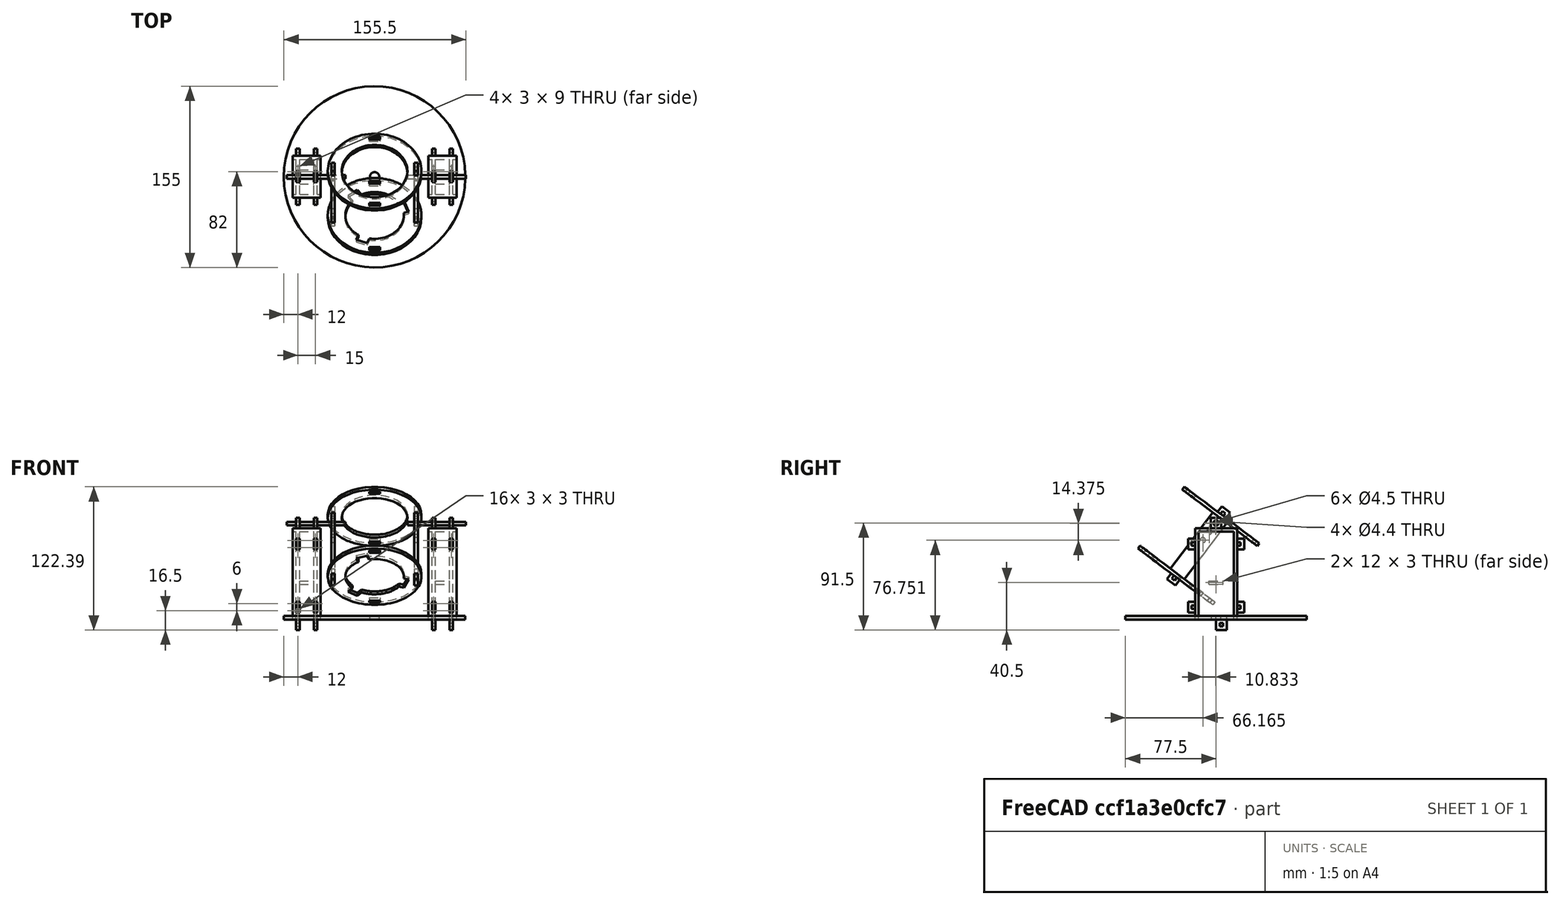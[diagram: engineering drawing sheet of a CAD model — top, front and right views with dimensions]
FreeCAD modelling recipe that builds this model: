
FCSTD DOCUMENT  (FreeCAD 0.16R6707 (Git))
Label: turretComplete
License: All rights reserved
LicenseURL: http://en.wikipedia.org/wiki/All_rights_reserved
objects: Part::Box×113, Part::Cut×80, Part::MultiFuse×19, Part::Cylinder×18
note: 230 computed .brp shape members not serialized (recipe doc carries the construction recipe); baked Part::Feature solids carry a one-line shape summary decoded from their .brp

FEATURE [Part::Cylinder] Cylinder
  Angle = 360
  Height = 3
  Radius = 77.5
FEATURE [Part::Cylinder] Cylinder017  label="Cylinder001"
  Angle = 360
  Height = 3
  Radius = 4
FEATURE [Part::Cut] Cut  label="cut002"
  Base = -> Cylinder
  Tool = -> Cylinder017
FEATURE [Part::Box] Box001  label="Cube001"
  Height = 3
  Length = 3
  Placement = pos=(-52,0,0) rot=(0,0,1;0rad)
  Width = 9
FEATURE [Part::Box] Box126  label="Cube048"
  Height = 3
  Length = 3
  Placement = pos=(-67,0,0) rot=(0,0,1;0rad)
  Width = 9
FEATURE [Part::Box] Box127  label="Cube049"
  Height = 3
  Length = 3
  Placement = pos=(49,0,0) rot=(0,0,1;0rad)
  Width = 9
FEATURE [Part::Box] Box128  label="Cube050"
  Height = 3
  Length = 3
  Placement = pos=(64,0,0) rot=(0,0,1;0rad)
  Width = 9
FEATURE [Part::Cut] Cut001
  Base = -> Cut
  Tool = -> Box126
FEATURE [Part::Cut] Cut002
  Base = -> Cut001
  Tool = -> Box001
FEATURE [Part::Cut] Cut003
  Base = -> Cut002
  Tool = -> Box128
FEATURE [Part::Cut] Cut004  label="turretBasis"
  Base = -> Cut003
  Tool = -> Box127
FEATURE [Part::Box] Box111  label="Cube033"
  Height = 3
  Length = 9
  Placement = pos=(1,12,15) rot=(0,0,1;0rad)
  Width = 3
FEATURE [Part::Box] Box112  label="Cube034"
  Height = 3
  Length = 9
  Placement = pos=(1,12,0) rot=(0,0,1;0rad)
  Width = 3
FEATURE [Part::Box] Box  label="Cube"
  Height = 12
  Length = 12
  Placement = pos=(-0.5,12,3) rot=(0,0,1;0rad)
  Width = 3
FEATURE [Part::MultiFuse] Fusion030  label="turretPitchHolderDistant"
  Placement = pos=(9.5,18,0) rot=(0,0,1;0rad)
  Shapes = -> [Box112,Box,Box111]
FEATURE [Part::Box] Box123  label="Cube045"
  Height = 3
  Length = 9
  Placement = pos=(10.5,-3,0) rot=(0,0,1;0rad)
  Width = 3
FEATURE [Part::Box] Box124  label="Cube046"
  Height = 24
  Length = 36
  Placement = pos=(-3,-3,-3) rot=(0,0,1;0rad)
  Width = 3
FEATURE [Part::Cut] Cut052
  Base = -> Box124
  Tool = -> Box123
FEATURE [Part::Box] Box125  label="Cube047"
  Height = 3
  Length = 9
  Placement = pos=(10.5,-3,15) rot=(0,0,1;0rad)
  Width = 3
FEATURE [Part::Cut] Cut058  label="turretPitchHolderTopPlate"
  Base = -> Cut052
  Placement = pos=(0,78,0) rot=(0,0,1;0rad)
  Tool = -> Box125
FEATURE [Part::Box] Box082  label="Cube006"
  Height = 3
  Length = 30
  Width = 75
FEATURE [Part::Box] Box129  label="Cube007"
  Height = 3
  Length = 9
  Placement = pos=(-9,6,0) rot=(0,0,1;0rad)
  Width = 9
FEATURE [Part::Box] Box002  label="Cube008"
  Height = 4
  Length = 3
  Placement = pos=(-6,9,0) rot=(0,0,1;0rad)
  Width = 3
FEATURE [Part::Cut] Cut034
  Base = -> Box129
  Tool = -> Box002
FEATURE [Part::Box] Box003  label="Cube009"
  Height = 3
  Length = 9
  Placement = pos=(-9,6,0) rot=(0,0,1;0rad)
  Width = 9
FEATURE [Part::Box] Box004  label="Cube010"
  Height = 4
  Length = 3
  Placement = pos=(-6,9,0) rot=(0,0,1;0rad)
  Width = 3
FEATURE [Part::Cut] Cut059
  Base = -> Box003
  Placement = pos=(39,0,0) rot=(0,0,1;0rad)
  Tool = -> Box004
FEATURE [Part::Box] Box005  label="Cube011"
  Height = 3
  Length = 9
  Placement = pos=(10.5,30,0) rot=(0,0,1;0rad)
  Width = 3
FEATURE [Part::Cut] Cut060
  Base = -> Box082
  Tool = -> Box005
FEATURE [Part::MultiFuse] Fusion027
  Shapes = -> [Cut034,Cut059,Cut060]
FEATURE [Part::Box] Box006  label="Cube012"
  Height = 3
  Length = 9
  Placement = pos=(10.5,36,0) rot=(0,0,1;0rad)
  Width = 9
FEATURE [Part::Cylinder] Cylinder027  label="RotationHoie"
  Angle = 360
  Height = 10
  Placement = pos=(15,40.5,0) rot=(0,0,1;0rad)
  Radius = 2.2
FEATURE [Part::Cut] Cut061
  Base = -> Box006
  Placement = pos=(0,42,0) rot=(0,0,1;0rad)
  Tool = -> Cylinder027
FEATURE [Part::Box] Box083  label="Cube013"
  Height = 3
  Length = 9
  Placement = pos=(-9,6,0) rot=(0,0,1;0rad)
  Width = 9
FEATURE [Part::Box] Box084  label="Cube014"
  Height = 4
  Length = 3
  Placement = pos=(-6,9,0) rot=(0,0,1;0rad)
  Width = 3
FEATURE [Part::Cut] Cut035
  Base = -> Box083
  Placement = pos=(24,-15,0) rot=(0,0,1;0rad)
  Tool = -> Box084
FEATURE [Part::Box] Box085  label="Cube015"
  Height = 3
  Length = 9
  Placement = pos=(-9,6,0) rot=(0,0,1;0rad)
  Width = 9
FEATURE [Part::Box] Box086  label="Cube016"
  Height = 4
  Length = 3
  Placement = pos=(-6,9,0) rot=(0,0,1;0rad)
  Width = 3
FEATURE [Part::Cut] Cut036
  Base = -> Box085
  Placement = pos=(39,54,0) rot=(0,0,1;0rad)
  Tool = -> Box086
FEATURE [Part::Box] Box087  label="Cube017"
  Height = 3
  Length = 9
  Placement = pos=(-9,6,0) rot=(0,0,1;0rad)
  Width = 9
FEATURE [Part::Box] Box088  label="Cube018"
  Height = 4
  Length = 3
  Placement = pos=(-6,9,0) rot=(0,0,1;0rad)
  Width = 3
FEATURE [Part::Cut] Cut037
  Base = -> Box087
  Placement = pos=(0,54,0) rot=(0,0,1;0rad)
  Tool = -> Box088
FEATURE [Part::MultiFuse] Fusion  label="Fusion001"
  Shapes = -> [Cut061,Cut035,Cut036,Cut037,Fusion027]
FEATURE [Part::Box] Box130  label="Cube051"
  Height = 3
  Length = 9
  Placement = pos=(10.5,75,0) rot=(0,0,1;0rad)
  Width = 3
FEATURE [Part::MultiFuse] Fusion031  label="turretPitchHolderSide"
  Shapes = -> [Fusion,Box130]
FEATURE [Part::Box] Box113  label="Cube035"
  Height = 3
  Length = 3
  Placement = pos=(30,60,0) rot=(0,0,1;0rad)
  Width = 9
FEATURE [Part::Box] Box114  label="Cube036"
  Height = 3
  Length = 3
  Placement = pos=(39,6,0) rot=(0,0,1;0rad)
  Width = 9
FEATURE [Part::Box] Box115  label="Cube037"
  Height = 3
  Length = 3
  Placement = pos=(39,6,15) rot=(0,0,1;0rad)
  Width = 9
FEATURE [Part::Box] Box116  label="Cube038"
  Height = 3
  Length = 3
  Placement = pos=(39,60,15) rot=(0,0,1;0rad)
  Width = 9
FEATURE [Part::Box] Box117  label="Cube039"
  Height = 24
  Length = 3
  Placement = pos=(39,0,-3) rot=(0,0,1;0rad)
  Width = 75
FEATURE [Part::Cut] Cut062
  Base = -> Box117
  Tool = -> Box116
FEATURE [Part::Cut] Cut045
  Base = -> Cut062
  Tool = -> Box115
FEATURE [Part::Cut] Cut046
  Base = -> Cut045
  Tool = -> Box114
FEATURE [Part::Cut] Cut047  label="Cutx058"
  Base = -> Cut046
  Placement = pos=(-9,0,0) rot=(0,0,1;0rad)
  Tool = -> Box113
FEATURE [Part::Cut] Cut063  label="turretPitchHolderSidePlate"
  Base = -> Cut047
  Tool = -> Box113
FEATURE [Part::Box] Box131  label="Cube052"
  Height = 3
  Length = 3
  Placement = pos=(30,60,0) rot=(0,0,1;0rad)
  Width = 9
FEATURE [Part::Box] Box132  label="Cube053"
  Height = 3
  Length = 3
  Placement = pos=(39,6,0) rot=(0,0,1;0rad)
  Width = 9
FEATURE [Part::Box] Box133  label="Cube054"
  Height = 3
  Length = 3
  Placement = pos=(39,6,15) rot=(0,0,1;0rad)
  Width = 9
FEATURE [Part::Box] Box134  label="Cube055"
  Height = 3
  Length = 3
  Placement = pos=(39,60,15) rot=(0,0,1;0rad)
  Width = 9
FEATURE [Part::Box] Box135  label="Cube056"
  Height = 24
  Length = 3
  Placement = pos=(39,0,-3) rot=(0,0,1;0rad)
  Width = 75
FEATURE [Part::Cut] Cut064
  Base = -> Box135
  Tool = -> Box134
FEATURE [Part::Cut] Cut065
  Base = -> Cut064
  Tool = -> Box133
FEATURE [Part::Cut] Cut066
  Base = -> Cut065
  Tool = -> Box132
FEATURE [Part::Cut] Cut067  label="Cutx059"
  Base = -> Cut066
  Placement = pos=(-9,0,0) rot=(0,0,1;0rad)
  Tool = -> Box131
FEATURE [Part::Cut] Cut068  label="turretPitchHolderSidePlate001"
  Base = -> Cut067
  Placement = pos=(-33,0,0) rot=(0,0,1;0rad)
  Tool = -> Box131
FEATURE [Part::Box] Box136  label="Cube057"
  Height = 3
  Length = 30
  Width = 75
FEATURE [Part::Box] Box137  label="Cube058"
  Height = 3
  Length = 9
  Placement = pos=(-9,6,0) rot=(0,0,1;0rad)
  Width = 9
FEATURE [Part::Box] Box138  label="Cube059"
  Height = 4
  Length = 3
  Placement = pos=(-6,9,0) rot=(0,0,1;0rad)
  Width = 3
FEATURE [Part::Cut] Cut069
  Base = -> Box137
  Tool = -> Box138
FEATURE [Part::Box] Box139  label="Cube060"
  Height = 3
  Length = 9
  Placement = pos=(-9,6,0) rot=(0,0,1;0rad)
  Width = 9
FEATURE [Part::Box] Box140  label="Cube061"
  Height = 4
  Length = 3
  Placement = pos=(-6,9,0) rot=(0,0,1;0rad)
  Width = 3
FEATURE [Part::Cut] Cut070
  Base = -> Box139
  Placement = pos=(39,0,0) rot=(0,0,1;0rad)
  Tool = -> Box140
FEATURE [Part::Box] Box141  label="Cube062"
  Height = 3
  Length = 9
  Placement = pos=(10.5,30,0) rot=(0,0,1;0rad)
  Width = 3
FEATURE [Part::Cut] Cut071
  Base = -> Box136
  Tool = -> Box141
FEATURE [Part::MultiFuse] Fusion032
  Shapes = -> [Cut069,Cut070,Cut071]
FEATURE [Part::Box] Box142  label="Cube063"
  Height = 3
  Length = 9
  Placement = pos=(10.5,36,0) rot=(0,0,1;0rad)
  Width = 9
FEATURE [Part::Cylinder] Cylinder028  label="RotationHoie001"
  Angle = 360
  Height = 10
  Placement = pos=(15,40.5,0) rot=(0,0,1;0rad)
  Radius = 2.2
FEATURE [Part::Cut] Cut072
  Base = -> Box142
  Placement = pos=(0,42,0) rot=(0,0,1;0rad)
  Tool = -> Cylinder028
FEATURE [Part::Box] Box143  label="Cube064"
  Height = 3
  Length = 9
  Placement = pos=(-9,6,0) rot=(0,0,1;0rad)
  Width = 9
FEATURE [Part::Box] Box144  label="Cube065"
  Height = 4
  Length = 3
  Placement = pos=(-6,9,0) rot=(0,0,1;0rad)
  Width = 3
FEATURE [Part::Cut] Cut073
  Base = -> Box143
  Placement = pos=(24,-15,0) rot=(0,0,1;0rad)
  Tool = -> Box144
FEATURE [Part::Box] Box145  label="Cube066"
  Height = 3
  Length = 9
  Placement = pos=(-9,6,0) rot=(0,0,1;0rad)
  Width = 9
FEATURE [Part::Box] Box146  label="Cube067"
  Height = 4
  Length = 3
  Placement = pos=(-6,9,0) rot=(0,0,1;0rad)
  Width = 3
FEATURE [Part::Cut] Cut074
  Base = -> Box145
  Placement = pos=(39,54,0) rot=(0,0,1;0rad)
  Tool = -> Box146
FEATURE [Part::Box] Box147  label="Cube068"
  Height = 3
  Length = 9
  Placement = pos=(-9,6,0) rot=(0,0,1;0rad)
  Width = 9
FEATURE [Part::Box] Box148  label="Cube069"
  Height = 4
  Length = 3
  Placement = pos=(-6,9,0) rot=(0,0,1;0rad)
  Width = 3
FEATURE [Part::Cut] Cut075
  Base = -> Box147
  Placement = pos=(0,54,0) rot=(0,0,1;0rad)
  Tool = -> Box148
FEATURE [Part::MultiFuse] Fusion033  label="Fusion035"
  Shapes = -> [Cut072,Cut073,Cut074,Cut075,Fusion032]
FEATURE [Part::Box] Box149  label="Cube070"
  Height = 3
  Length = 9
  Placement = pos=(10.5,75,0) rot=(0,0,1;0rad)
  Width = 3
FEATURE [Part::MultiFuse] Fusion034  label="turretPitchHolderSide001"
  Placement = pos=(0,0,15) rot=(0,0,1;0rad)
  Shapes = -> [Fusion033,Box149]
FEATURE [Part::MultiFuse] Fusion035  label="turretPitchHolder"
  Placement = pos=(49,-15,0) rot=(0.57735,0.57735,0.57735;2.0944rad)
  Shapes = -> [Fusion030,Cut058,Fusion031,Cut063,Cut068,Fusion034]
FEATURE [Part::Box] Box150  label="Cube071"
  Height = 3
  Length = 9
  Placement = pos=(1,12,15) rot=(0,0,1;0rad)
  Width = 3
FEATURE [Part::Box] Box151  label="Cube072"
  Height = 3
  Length = 9
  Placement = pos=(1,12,0) rot=(0,0,1;0rad)
  Width = 3
FEATURE [Part::Box] Box152  label="Cube073"
  Height = 12
  Length = 12
  Placement = pos=(-0.5,12,3) rot=(0,0,1;0rad)
  Width = 3
FEATURE [Part::MultiFuse] Fusion036  label="turretPitchHolderDistant001"
  Placement = pos=(9.5,18,0) rot=(0,0,1;0rad)
  Shapes = -> [Box151,Box152,Box150]
FEATURE [Part::Box] Box153  label="Cube074"
  Height = 3
  Length = 9
  Placement = pos=(10.5,-3,0) rot=(0,0,1;0rad)
  Width = 3
FEATURE [Part::Box] Box154  label="Cube075"
  Height = 24
  Length = 36
  Placement = pos=(-3,-3,-3) rot=(0,0,1;0rad)
  Width = 3
FEATURE [Part::Cut] Cut076
  Base = -> Box154
  Tool = -> Box153
FEATURE [Part::Box] Box155  label="Cube076"
  Height = 3
  Length = 9
  Placement = pos=(10.5,-3,15) rot=(0,0,1;0rad)
  Width = 3
FEATURE [Part::Cut] Cut077  label="turretPitchHolderTopPlate001"
  Base = -> Cut076
  Placement = pos=(0,78,0) rot=(0,0,1;0rad)
  Tool = -> Box155
FEATURE [Part::Box] Box156  label="Cube077"
  Height = 3
  Length = 30
  Width = 75
FEATURE [Part::Box] Box157  label="Cube078"
  Height = 3
  Length = 9
  Placement = pos=(-9,6,0) rot=(0,0,1;0rad)
  Width = 9
FEATURE [Part::Box] Box158  label="Cube079"
  Height = 4
  Length = 3
  Placement = pos=(-6,9,0) rot=(0,0,1;0rad)
  Width = 3
FEATURE [Part::Cut] Cut078
  Base = -> Box157
  Tool = -> Box158
FEATURE [Part::Box] Box159  label="Cube080"
  Height = 3
  Length = 9
  Placement = pos=(-9,6,0) rot=(0,0,1;0rad)
  Width = 9
FEATURE [Part::Box] Box160  label="Cube081"
  Height = 4
  Length = 3
  Placement = pos=(-6,9,0) rot=(0,0,1;0rad)
  Width = 3
FEATURE [Part::Cut] Cut079
  Base = -> Box159
  Placement = pos=(39,0,0) rot=(0,0,1;0rad)
  Tool = -> Box160
FEATURE [Part::Box] Box161  label="Cube082"
  Height = 3
  Length = 9
  Placement = pos=(10.5,30,0) rot=(0,0,1;0rad)
  Width = 3
FEATURE [Part::Cut] Cut080
  Base = -> Box156
  Tool = -> Box161
FEATURE [Part::MultiFuse] Fusion037
  Shapes = -> [Cut078,Cut079,Cut080]
FEATURE [Part::Box] Box162  label="Cube083"
  Height = 3
  Length = 9
  Placement = pos=(10.5,36,0) rot=(0,0,1;0rad)
  Width = 9
FEATURE [Part::Cylinder] Cylinder029  label="RotationHoie002"
  Angle = 360
  Height = 10
  Placement = pos=(15,40.5,0) rot=(0,0,1;0rad)
  Radius = 2.2
FEATURE [Part::Cut] Cut081
  Base = -> Box162
  Placement = pos=(0,42,0) rot=(0,0,1;0rad)
  Tool = -> Cylinder029
FEATURE [Part::Box] Box163  label="Cube084"
  Height = 3
  Length = 9
  Placement = pos=(-9,6,0) rot=(0,0,1;0rad)
  Width = 9
FEATURE [Part::Box] Box164  label="Cube085"
  Height = 4
  Length = 3
  Placement = pos=(-6,9,0) rot=(0,0,1;0rad)
  Width = 3
FEATURE [Part::Cut] Cut082
  Base = -> Box163
  Placement = pos=(24,-15,0) rot=(0,0,1;0rad)
  Tool = -> Box164
FEATURE [Part::Box] Box165  label="Cube086"
  Height = 3
  Length = 9
  Placement = pos=(-9,6,0) rot=(0,0,1;0rad)
  Width = 9
FEATURE [Part::Box] Box166  label="Cube087"
  Height = 4
  Length = 3
  Placement = pos=(-6,9,0) rot=(0,0,1;0rad)
  Width = 3
FEATURE [Part::Cut] Cut083
  Base = -> Box165
  Placement = pos=(39,54,0) rot=(0,0,1;0rad)
  Tool = -> Box166
FEATURE [Part::Box] Box167  label="Cube088"
  Height = 3
  Length = 9
  Placement = pos=(-9,6,0) rot=(0,0,1;0rad)
  Width = 9
FEATURE [Part::Box] Box168  label="Cube089"
  Height = 4
  Length = 3
  Placement = pos=(-6,9,0) rot=(0,0,1;0rad)
  Width = 3
FEATURE [Part::Cut] Cut084
  Base = -> Box167
  Placement = pos=(0,54,0) rot=(0,0,1;0rad)
  Tool = -> Box168
FEATURE [Part::MultiFuse] Fusion038  label="Fusion044"
  Shapes = -> [Cut081,Cut082,Cut083,Cut084,Fusion037]
FEATURE [Part::Box] Box169  label="Cube090"
  Height = 3
  Length = 9
  Placement = pos=(10.5,75,0) rot=(0,0,1;0rad)
  Width = 3
FEATURE [Part::MultiFuse] Fusion039  label="turretPitchHolderSide002"
  Shapes = -> [Fusion038,Box169]
FEATURE [Part::Box] Box170  label="Cube091"
  Height = 3
  Length = 3
  Placement = pos=(30,60,0) rot=(0,0,1;0rad)
  Width = 9
FEATURE [Part::Box] Box171  label="Cube092"
  Height = 3
  Length = 3
  Placement = pos=(39,6,0) rot=(0,0,1;0rad)
  Width = 9
FEATURE [Part::Box] Box172  label="Cube093"
  Height = 3
  Length = 3
  Placement = pos=(39,6,15) rot=(0,0,1;0rad)
  Width = 9
FEATURE [Part::Box] Box173  label="Cube094"
  Height = 3
  Length = 3
  Placement = pos=(39,60,15) rot=(0,0,1;0rad)
  Width = 9
FEATURE [Part::Box] Box174  label="Cube095"
  Height = 24
  Length = 3
  Placement = pos=(39,0,-3) rot=(0,0,1;0rad)
  Width = 75
FEATURE [Part::Cut] Cut085
  Base = -> Box174
  Tool = -> Box173
FEATURE [Part::Cut] Cut086
  Base = -> Cut085
  Tool = -> Box172
FEATURE [Part::Cut] Cut087
  Base = -> Cut086
  Tool = -> Box171
FEATURE [Part::Cut] Cut088  label="Cutx060"
  Base = -> Cut087
  Placement = pos=(-9,0,0) rot=(0,0,1;0rad)
  Tool = -> Box170
FEATURE [Part::Cut] Cut089  label="turretPitchHolderSidePlate002"
  Base = -> Cut088
  Tool = -> Box170
FEATURE [Part::Box] Box175  label="Cube096"
  Height = 3
  Length = 3
  Placement = pos=(30,60,0) rot=(0,0,1;0rad)
  Width = 9
FEATURE [Part::Box] Box176  label="Cube097"
  Height = 3
  Length = 3
  Placement = pos=(39,6,0) rot=(0,0,1;0rad)
  Width = 9
FEATURE [Part::Box] Box177  label="Cube098"
  Height = 3
  Length = 3
  Placement = pos=(39,6,15) rot=(0,0,1;0rad)
  Width = 9
FEATURE [Part::Box] Box178  label="Cube099"
  Height = 3
  Length = 3
  Placement = pos=(39,60,15) rot=(0,0,1;0rad)
  Width = 9
FEATURE [Part::Box] Box179  label="Cube100"
  Height = 24
  Length = 3
  Placement = pos=(39,0,-3) rot=(0,0,1;0rad)
  Width = 75
FEATURE [Part::Cut] Cut090
  Base = -> Box179
  Tool = -> Box178
FEATURE [Part::Cut] Cut091
  Base = -> Cut090
  Tool = -> Box177
FEATURE [Part::Cut] Cut092
  Base = -> Cut091
  Tool = -> Box176
FEATURE [Part::Cut] Cut093  label="Cutx061"
  Base = -> Cut092
  Placement = pos=(-9,0,0) rot=(0,0,1;0rad)
  Tool = -> Box175
FEATURE [Part::Cut] Cut094  label="turretPitchHolderSidePlate003"
  Base = -> Cut093
  Placement = pos=(-33,0,0) rot=(0,0,1;0rad)
  Tool = -> Box175
FEATURE [Part::Box] Box180  label="Cube101"
  Height = 3
  Length = 30
  Width = 75
FEATURE [Part::Box] Box181  label="Cube102"
  Height = 3
  Length = 9
  Placement = pos=(-9,6,0) rot=(0,0,1;0rad)
  Width = 9
FEATURE [Part::Box] Box182  label="Cube103"
  Height = 4
  Length = 3
  Placement = pos=(-6,9,0) rot=(0,0,1;0rad)
  Width = 3
FEATURE [Part::Cut] Cut095
  Base = -> Box181
  Tool = -> Box182
FEATURE [Part::Box] Box183  label="Cube104"
  Height = 3
  Length = 9
  Placement = pos=(-9,6,0) rot=(0,0,1;0rad)
  Width = 9
FEATURE [Part::Box] Box184  label="Cube105"
  Height = 4
  Length = 3
  Placement = pos=(-6,9,0) rot=(0,0,1;0rad)
  Width = 3
FEATURE [Part::Cut] Cut096
  Base = -> Box183
  Placement = pos=(39,0,0) rot=(0,0,1;0rad)
  Tool = -> Box184
FEATURE [Part::Box] Box185  label="Cube106"
  Height = 3
  Length = 9
  Placement = pos=(10.5,30,0) rot=(0,0,1;0rad)
  Width = 3
FEATURE [Part::Cut] Cut097
  Base = -> Box180
  Tool = -> Box185
FEATURE [Part::MultiFuse] Fusion040
  Shapes = -> [Cut095,Cut096,Cut097]
FEATURE [Part::Box] Box186  label="Cube107"
  Height = 3
  Length = 9
  Placement = pos=(10.5,36,0) rot=(0,0,1;0rad)
  Width = 9
FEATURE [Part::Cylinder] Cylinder030  label="RotationHoie003"
  Angle = 360
  Height = 10
  Placement = pos=(15,40.5,0) rot=(0,0,1;0rad)
  Radius = 2.2
FEATURE [Part::Cut] Cut098
  Base = -> Box186
  Placement = pos=(0,42,0) rot=(0,0,1;0rad)
  Tool = -> Cylinder030
FEATURE [Part::Box] Box187  label="Cube108"
  Height = 3
  Length = 9
  Placement = pos=(-9,6,0) rot=(0,0,1;0rad)
  Width = 9
FEATURE [Part::Box] Box188  label="Cube109"
  Height = 4
  Length = 3
  Placement = pos=(-6,9,0) rot=(0,0,1;0rad)
  Width = 3
FEATURE [Part::Cut] Cut099
  Base = -> Box187
  Placement = pos=(24,-15,0) rot=(0,0,1;0rad)
  Tool = -> Box188
FEATURE [Part::Box] Box189  label="Cube110"
  Height = 3
  Length = 9
  Placement = pos=(-9,6,0) rot=(0,0,1;0rad)
  Width = 9
FEATURE [Part::Box] Box190  label="Cube111"
  Height = 4
  Length = 3
  Placement = pos=(-6,9,0) rot=(0,0,1;0rad)
  Width = 3
FEATURE [Part::Cut] Cut100
  Base = -> Box189
  Placement = pos=(39,54,0) rot=(0,0,1;0rad)
  Tool = -> Box190
FEATURE [Part::Box] Box191  label="Cube112"
  Height = 3
  Length = 9
  Placement = pos=(-9,6,0) rot=(0,0,1;0rad)
  Width = 9
FEATURE [Part::Box] Box192  label="Cube113"
  Height = 4
  Length = 3
  Placement = pos=(-6,9,0) rot=(0,0,1;0rad)
  Width = 3
FEATURE [Part::Cut] Cut101
  Base = -> Box191
  Placement = pos=(0,54,0) rot=(0,0,1;0rad)
  Tool = -> Box192
FEATURE [Part::MultiFuse] Fusion041  label="Fusion045"
  Shapes = -> [Cut098,Cut099,Cut100,Cut101,Fusion040]
FEATURE [Part::Box] Box193  label="Cube114"
  Height = 3
  Length = 9
  Placement = pos=(10.5,75,0) rot=(0,0,1;0rad)
  Width = 3
FEATURE [Part::MultiFuse] Fusion042  label="turretPitchHolderSide003"
  Placement = pos=(0,0,15) rot=(0,0,1;0rad)
  Shapes = -> [Fusion041,Box193]
FEATURE [Part::MultiFuse] Fusion043  label="turretPitchHolder001"
  Placement = pos=(-67,-15,0) rot=(0.57735,0.57735,0.57735;2.0944rad)
  Shapes = -> [Fusion036,Cut077,Fusion039,Cut089,Cut094,Fusion042]
FEATURE [Part::Cylinder] Cylinder031
  Angle = 360
  Height = 3
  Radius = 40
FEATURE [Part::Cylinder] Cylinder001  label="Cylinder032"
  Angle = 360
  Height = 3
  Radius = 25
FEATURE [Part::Cut] Cut102
  Base = -> Cylinder031
  Tool = -> Cylinder001
FEATURE [Part::Box] Box194  label="Cube115"
  Height = 3
  Length = 3
  Placement = pos=(34,-4.5,0) rot=(0,0,1;0rad)
  Width = 9
FEATURE [Part::Box] Box195  label="Cube116"
  Height = 3
  Length = 3
  Placement = pos=(-37,-4.5,0) rot=(0,0,1;0rad)
  Width = 9
FEATURE [Part::Cut] Cut103
  Base = -> Cut102
  Tool = -> Box194
FEATURE [Part::Cut] Cut104
  Base = -> Cut103
  Tool = -> Box195
FEATURE [Part::Box] Box196  label="Cube002"
  Height = 3
  Length = 9
  Placement = pos=(-4.5,34,0) rot=(0,0,1;0rad)
  Width = 3
FEATURE [Part::Box] Box197  label="Cube003"
  Height = 3
  Length = 9
  Placement = pos=(-4.5,-37,0) rot=(0,0,1;0rad)
  Width = 3
FEATURE [Part::Cut] Cut105
  Base = -> Cut104
  Tool = -> Box196
FEATURE [Part::Cut] Cut106  label="RingBasis"
  Base = -> Cut105
  Tool = -> Box197
FEATURE [Part::Cylinder] Cylinder002
  Angle = 360
  Height = 3
  Radius = 40
FEATURE [Part::Cylinder] Cylinder003
  Angle = 360
  Height = 3
  Radius = 28
FEATURE [Part::Cut] Cut005
  Base = -> Cylinder002
  Tool = -> Cylinder003
FEATURE [Part::Box] Box198  label="Cube004"
  Height = 3
  Length = 3
  Placement = pos=(34,-4.5,0) rot=(0,0,1;0rad)
  Width = 9
FEATURE [Part::Box] Box199  label="Cube005"
  Height = 3
  Length = 3
  Placement = pos=(-37,-4.5,0) rot=(0,0,1;0rad)
  Width = 9
FEATURE [Part::Cut] Cut006
  Base = -> Cut005
  Tool = -> Box198
FEATURE [Part::Cut] Cut007
  Base = -> Cut006
  Tool = -> Box199
FEATURE [Part::Box] Box200  label="Cube117"
  Height = 3
  Length = 9
  Placement = pos=(-4.5,34,0) rot=(0,0,1;0rad)
  Width = 3
FEATURE [Part::Box] Box007  label="Cube118"
  Height = 3
  Length = 9
  Placement = pos=(-4.5,-37,0) rot=(0,0,1;0rad)
  Width = 3
FEATURE [Part::Cut] Cut008
  Base = -> Cut007
  Tool = -> Box200
FEATURE [Part::Cut] Cut009  label="RingMiddle"
  Base = -> Cut008
  Placement = pos=(0,0,-63) rot=(0,0,1;0rad)
  Tool = -> Box007
FEATURE [Part::Box] Box019  label="Cube019"
  Height = 3
  Length = 12
  Placement = pos=(-6,1,0) rot=(0,0,-1;0.349066rad)
  Width = 30
FEATURE [Part::Box] Box020  label="Cube020"
  Height = 3
  Length = 10
  Placement = pos=(2,-5,0) rot=(0,0,1;1.93731rad)
  Width = 30
FEATURE [Part::Box] Box021  label="Cube021"
  Height = 3
  Length = 10
  Placement = pos=(3,3,0) rot=(0,0,1;4.08407rad)
  Width = 30
FEATURE [Part::Cut] Cut020
  Base = -> Cut106
  Tool = -> Box019
FEATURE [Part::Cut] Cut021
  Base = -> Cut020
  Tool = -> Box021
FEATURE [Part::Cut] Cut022  label="RingBasis001"
  Base = -> Cut021
  Tool = -> Box020
FEATURE [Part::Box] Box009  label="Cube119"
  Height = 9
  Length = 9
  Placement = pos=(-4.5,-66,3) rot=(0,0,1;0rad)
  Width = 3
FEATURE [Part::Box] Box010  label="Cube120"
  Height = 3
  Length = 3
  Placement = pos=(-1.5,-66,6) rot=(0,0,1;0rad)
  Width = 3
FEATURE [Part::Cut] Cut010
  Base = -> Box009
  Placement = pos=(0,0,30) rot=(0,0,1;0rad)
  Tool = -> Box010
FEATURE [Part::Box] Box011  label="Cube121"
  Height = 60
  Length = 15
  Placement = pos=(-7.5,-66,-27) rot=(0,0,1;0rad)
  Width = 3
FEATURE [Part::Box] Box012  label="Cube122"
  Height = 9
  Length = 9
  Placement = pos=(-4.5,-66,3) rot=(0,0,1;0rad)
  Width = 3
FEATURE [Part::Box] Box013  label="Cube123"
  Height = 3
  Length = 3
  Placement = pos=(-1.5,-66,6) rot=(0,0,1;0rad)
  Width = 3
FEATURE [Part::Cut] Cut011
  Base = -> Box012
  Placement = pos=(0,0,-39) rot=(0,0,1;0rad)
  Tool = -> Box013
FEATURE [Part::MultiFuse] Fusion044  label="Fusion048"
  Shapes = -> [Cut011,Box011,Cut010]
FEATURE [Part::Cylinder] Cylinder004
  Angle = 360
  Height = 3
  Placement = pos=(0,-63,-12) rot=(1,0,0;1.5708rad)
  Radius = 2.25
FEATURE [Part::Cylinder] Cylinder005
  Angle = 360
  Height = 3
  Placement = pos=(0,-63,-3) rot=(1,0,0;1.5708rad)
  Radius = 2.25
FEATURE [Part::Cylinder] Cylinder006
  Angle = 360
  Height = 3
  Placement = pos=(0,-63,-21) rot=(1,0,0;1.5708rad)
  Radius = 2.25
FEATURE [Part::Cut] Cut012
  Base = -> Fusion044
  Tool = -> Cylinder004
FEATURE [Part::Cut] Cut013
  Base = -> Cut012
  Tool = -> Cylinder006
FEATURE [Part::Cut] Cut014  label="pitchRingConnector"
  Base = -> Cut013
  Placement = pos=(0,29,-33) rot=(0,0,1;0rad)
  Tool = -> Cylinder005
FEATURE [Part::Box] Box022  label="Cube022"
  Height = 9
  Length = 9
  Placement = pos=(-4.5,-66,3) rot=(0,0,1;0rad)
  Width = 3
FEATURE [Part::Box] Box023  label="Cube023"
  Height = 3
  Length = 3
  Placement = pos=(-1.5,-66,6) rot=(0,0,1;0rad)
  Width = 3
FEATURE [Part::Cut] Cut023
  Base = -> Box022
  Placement = pos=(0,0,30) rot=(0,0,1;0rad)
  Tool = -> Box023
FEATURE [Part::Box] Box024  label="Cube024"
  Height = 60
  Length = 15
  Placement = pos=(-7.5,-66,-27) rot=(0,0,1;0rad)
  Width = 3
FEATURE [Part::Box] Box025  label="Cube025"
  Height = 9
  Length = 9
  Placement = pos=(-4.5,-66,3) rot=(0,0,1;0rad)
  Width = 3
FEATURE [Part::Box] Box026  label="Cube026"
  Height = 3
  Length = 3
  Placement = pos=(-1.5,-66,6) rot=(0,0,1;0rad)
  Width = 3
FEATURE [Part::Cut] Cut024
  Base = -> Box025
  Placement = pos=(0,0,-39) rot=(0,0,1;0rad)
  Tool = -> Box026
FEATURE [Part::MultiFuse] Fusion001  label="Fusion049"
  Shapes = -> [Cut024,Box024,Cut023]
FEATURE [Part::Cylinder] Cylinder007
  Angle = 360
  Height = 3
  Placement = pos=(0,-63,-12) rot=(1,0,0;1.5708rad)
  Radius = 2.25
FEATURE [Part::Cylinder] Cylinder008
  Angle = 360
  Height = 3
  Placement = pos=(0,-63,-3) rot=(1,0,0;1.5708rad)
  Radius = 2.25
FEATURE [Part::Cylinder] Cylinder009
  Angle = 360
  Height = 3
  Placement = pos=(0,-63,-21) rot=(1,0,0;1.5708rad)
  Radius = 2.25
FEATURE [Part::Cut] Cut025
  Base = -> Fusion001
  Tool = -> Cylinder007
FEATURE [Part::Cut] Cut026
  Base = -> Cut025
  Tool = -> Cylinder009
FEATURE [Part::Cut] Cut027  label="pitchRingConnector001"
  Base = -> Cut026
  Placement = pos=(0,100,-33) rot=(0,0,1;0rad)
  Tool = -> Cylinder008
FEATURE [Part::MultiFuse] Fusion045  label="turretPitch"
  Placement = pos=(0,-33,39) rot=(0.68811,0.68811,-0.230238;2.689rad)
  Shapes = -> [Cut009,Cut022,Cut014,Cut027]
FEATURE [Part::Cylinder] Cylinder032  label="Cylinder033"
  Angle = 360
  Height = 50
  Placement = pos=(28,0,82) rot=(0,1,0;1.5708rad)
  Radius = 1.5
FEATURE [Part::Cylinder] Cylinder033  label="Cylinder034"
  Angle = 360
  Height = 50
  Placement = pos=(-75,0,82) rot=(0,1,0;1.5708rad)
  Radius = 1.5
